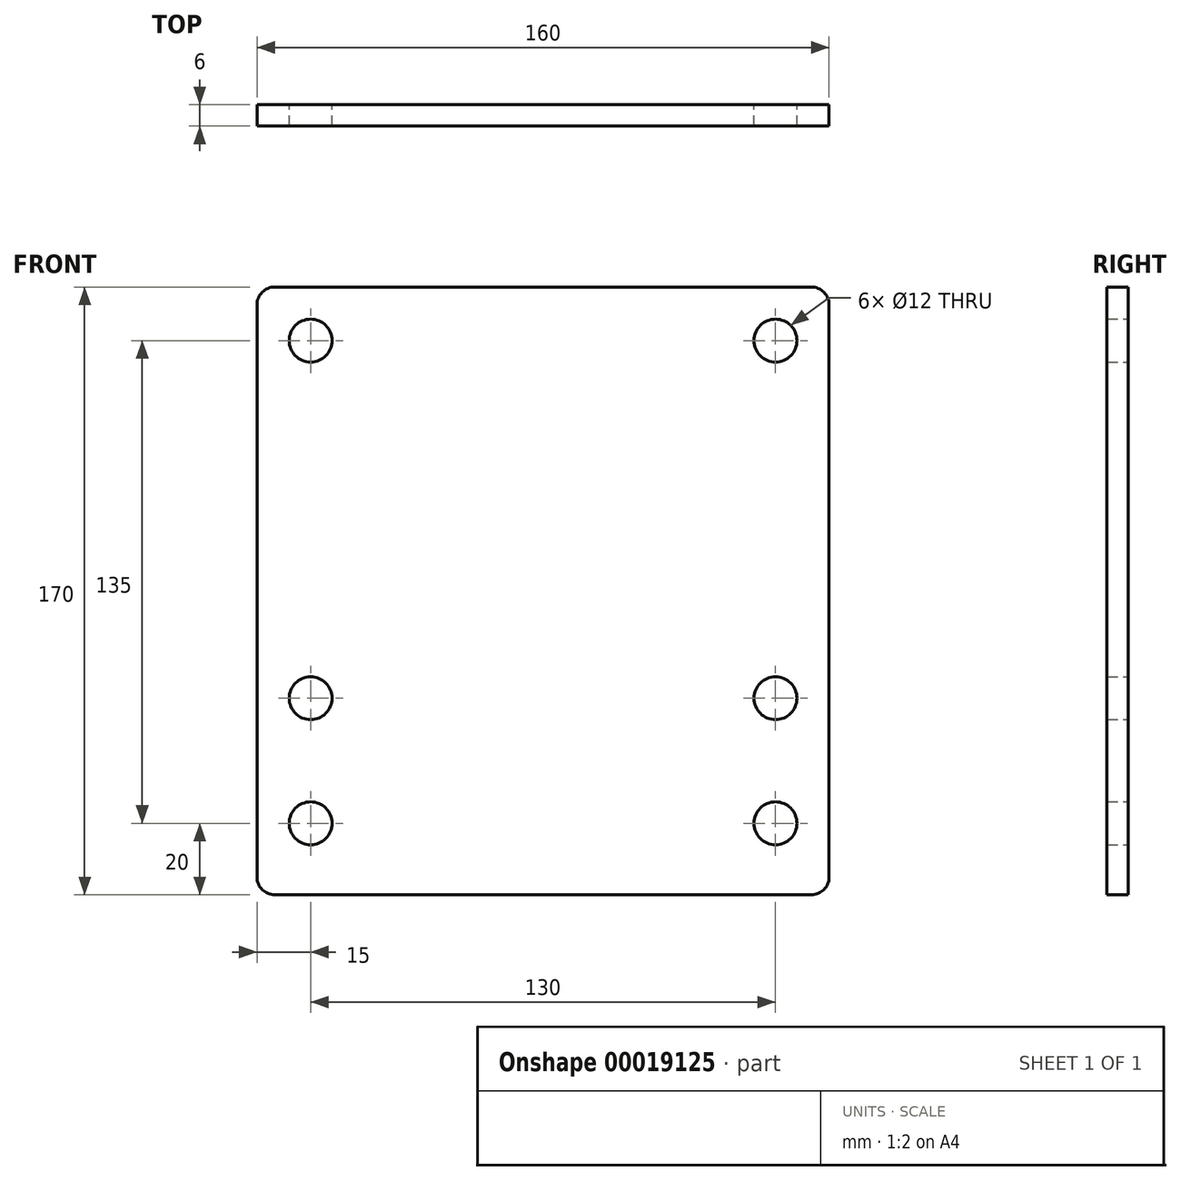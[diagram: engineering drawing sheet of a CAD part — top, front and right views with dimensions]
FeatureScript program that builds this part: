
annotation { "Feature Type Name" : "Feature", "Feature Type Description" : "" }
export const myFeature = defineFeature(function(context is Context, id is Id, definition is map)
    precondition{}
    {
        {
            var Q0;
            Q0=qCreatedBy(makeId("Front.planeOp"),FACE);
            var sketch = newSketch(context, id + "F0", { "sketchPlane" : qUnion([Q0])});
            skLineSegment(sketch, "E0.rect.bottom", {"start": v(75, -85) * mm, "end": v(-75, -85) * mm});
            skLineSegment(sketch, "E0.rect.top", {"start": v(75, 85) * mm, "end": v(-75, 85) * mm});
            skLineSegment(sketch, "E0.rect.left", {"start": v(80, -80) * mm, "end": v(80, 80) * mm});
            skLineSegment(sketch, "E0.rect.right", {"start": v(-80, -80) * mm, "end": v(-80, 80) * mm});
            skPoint(sketch, "E0.rect.middle", {"position": v(0, 0) * mm});
            skCircle(sketch, "E1", {"center": v(-65, 70) * mm, "radius": 6 * mm});
            skCircle(sketch, "E2", {"center": v(-65, -30) * mm, "radius": 6 * mm});
            skCircle(sketch, "E3", {"center": v(-65, -65) * mm, "radius": 6 * mm});
            skLineSegment(sketch, "E4", {"start": v(-65, 85) * mm, "end": v(-65, -85) * mm, "construction": true});
            skLineSegment(sketch, "E5", {"start": v(0, 85) * mm, "end": v(0, -85) * mm, "construction": true});
            skCircle(sketch, "E6.MirrorC", {"center": v(65, 70) * mm, "radius": 6 * mm});
            skCircle(sketch, "E7.MirrorC", {"center": v(65, -30) * mm, "radius": 6 * mm});
            skCircle(sketch, "E8.MirrorC", {"center": v(65, -65) * mm, "radius": 6 * mm});
            skPoint(sketch, "E9.visualSharp", {"position": v(80, 85) * mm});
            skArc(sketch, "E9.filletArc", {"start": v(80, 80) * mm, "mid": v(78.54, 83.54) * mm, "end": v(75, 85) * mm});
            skPoint(sketch, "E10.visualSharp", {"position": v(-80, 85) * mm});
            skArc(sketch, "E10.filletArc", {"start": v(-75, 85) * mm, "mid": v(-78.54, 83.54) * mm, "end": v(-80, 80) * mm});
            skPoint(sketch, "E11.visualSharp", {"position": v(80, -85) * mm});
            skArc(sketch, "E11.filletArc", {"start": v(75, -85) * mm, "mid": v(78.54, -83.54) * mm, "end": v(80, -80) * mm});
            skPoint(sketch, "E12.visualSharp", {"position": v(-80, -85) * mm});
            skArc(sketch, "E12.filletArc", {"start": v(-80, -80) * mm, "mid": v(-78.54, -83.54) * mm, "end": v(-75, -85) * mm});
            skSolve(sketch);
        }
        {
            var Q0;
            Q0 = qSketchRegion(id + "F0", true);
            extrude(context, id + "F1", {"entities" : qUnion([Q0]), "depth" : 6 * mm});
        }
    });
